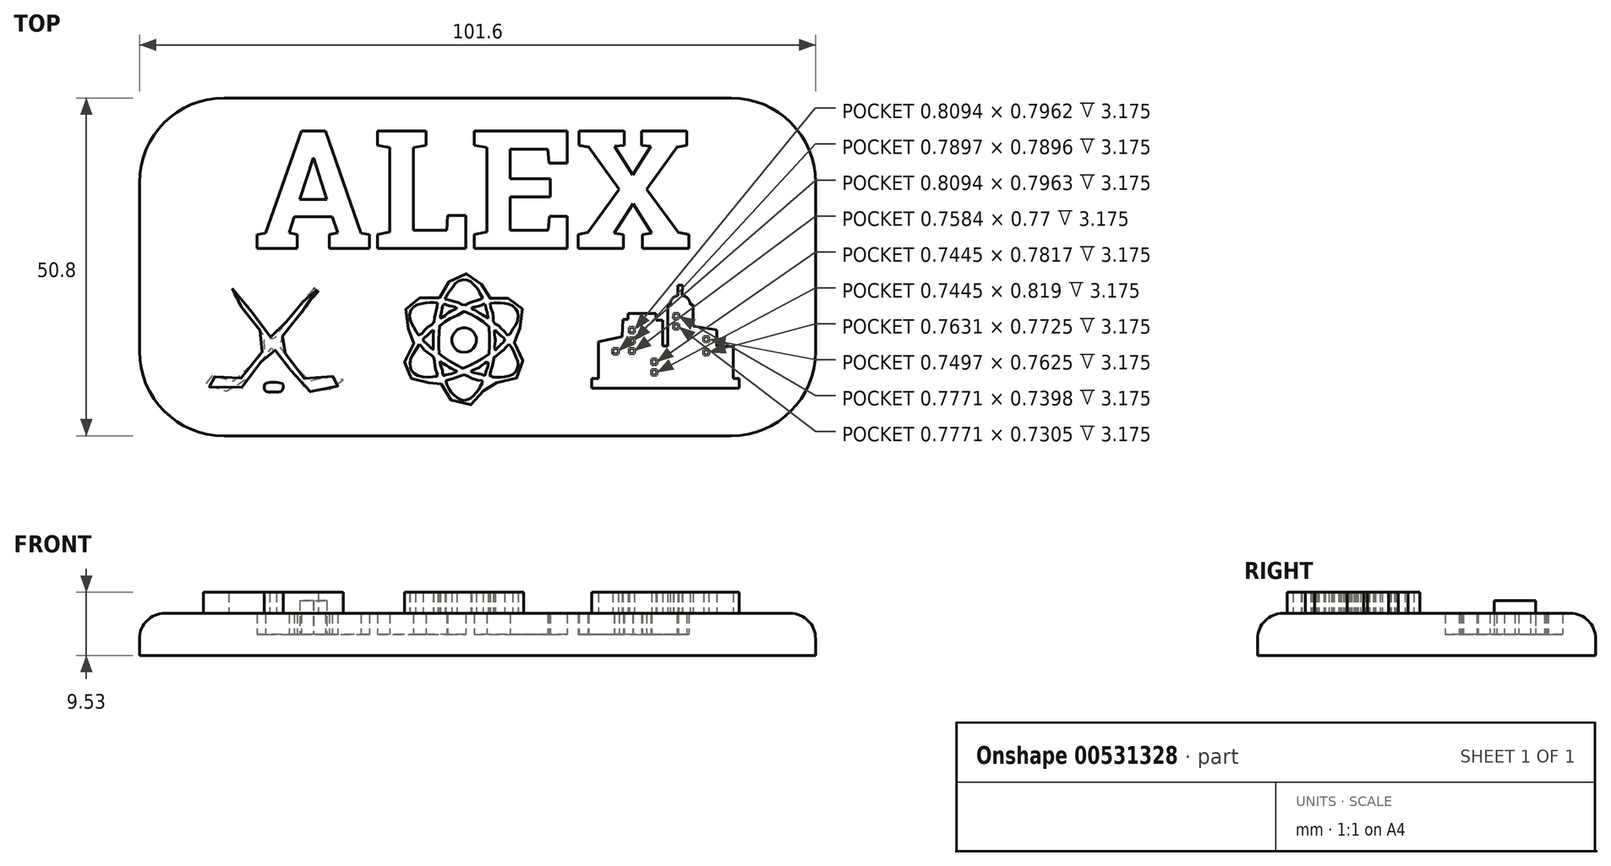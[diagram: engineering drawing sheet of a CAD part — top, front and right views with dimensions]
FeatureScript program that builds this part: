
annotation { "Feature Type Name" : "Feature", "Feature Type Description" : "" }
export const myFeature = defineFeature(function(context is Context, id is Id, definition is map)
    precondition{}
    {
        {
            var Q0;
            Q0=qCreatedBy(makeId("Top.planeOp"),FACE);
            var sketch = newSketch(context, id + "F0", { "sketchPlane" : qUnion([Q0])});
            skLineSegment(sketch, "E0", {"start": v(-38.91, 22.63) * mm, "end": v(37.29, 22.63) * mm});
            skLineSegment(sketch, "E1", {"start": v(49.99, 9.93) * mm, "end": v(49.99, -15.47) * mm});
            skLineSegment(sketch, "E2", {"start": v(-51.61, 9.93) * mm, "end": v(-51.61, -15.47) * mm});
            skLineSegment(sketch, "E3", {"start": v(-38.91, -28.17) * mm, "end": v(37.29, -28.17) * mm});
            skPoint(sketch, "E4.visualSharp", {"position": v(-51.61, 22.63) * mm});
            skArc(sketch, "E4.filletArc", {"start": v(-38.91, 22.63) * mm, "mid": v(-47.9, 18.91) * mm, "end": v(-51.61, 9.93) * mm});
            skPoint(sketch, "E5.visualSharp", {"position": v(49.99, 22.63) * mm});
            skArc(sketch, "E5.filletArc", {"start": v(49.99, 9.93) * mm, "mid": v(46.27, 18.91) * mm, "end": v(37.29, 22.63) * mm});
            skPoint(sketch, "E6.visualSharp", {"position": v(49.99, -28.17) * mm});
            skArc(sketch, "E6.filletArc", {"start": v(37.29, -28.17) * mm, "mid": v(46.27, -24.45) * mm, "end": v(49.99, -15.47) * mm});
            skPoint(sketch, "E7.visualSharp", {"position": v(-51.61, -28.17) * mm});
            skArc(sketch, "E7.filletArc", {"start": v(-51.61, -15.47) * mm, "mid": v(-47.9, -24.45) * mm, "end": v(-38.91, -28.17) * mm});
            skText(sketch, "E8", { "text": "ALEX", "fontName": "RobotoSlab-Bold.ttf"});
            const initialGuessF0  = {"E8": [-0.03442, 0, 1, 0, 0.0179]};
            skSetInitialGuess(sketch, initialGuessF0);
            skSolve(sketch);
        }
        {
            var Q0;
            Q0=makeQuery(id+"F0.imprint","IMPRINT",FACE,{"disambiguationData":[TD([[makeQuery(id+"F0.imprint","IMPRINT",EDGE,{"derivedFrom":sQuery(id+"F0.wireOp",EDGE,"E0")}),-1.0]])]});
            extrude(context, id + "F1", {"entities" : qUnion([Q0]), "depth" : 6.35 * mm, "offsetDistance" : 25.4 * mm});
        }
        {
            var Q0;
            Q0=makeQuery(id+"F1.opExtrude","CAP_EDGE",EDGE,{"disambiguationData":[OSD([sQuery(id+"F0.wireOp",EDGE,"E4.filletArc")])],"isStart":false});
            var Q1;
            Q1=makeQuery(id+"F1.opExtrude","CAP_EDGE",EDGE,{"disambiguationData":[OSD([sQuery(id+"F0.wireOp",EDGE,"E0")])],"isStart":false});
            var Q2;
            Q2=makeQuery(id+"F1.opExtrude","CAP_EDGE",EDGE,{"disambiguationData":[OSD([sQuery(id+"F0.wireOp",EDGE,"E5.filletArc")])],"isStart":false});
            var Q3;
            Q3=makeQuery(id+"F1.opExtrude","CAP_EDGE",EDGE,{"disambiguationData":[OSD([sQuery(id+"F0.wireOp",EDGE,"E1")])],"isStart":false});
            var Q4;
            Q4=makeQuery(id+"F1.opExtrude","CAP_EDGE",EDGE,{"disambiguationData":[OSD([sQuery(id+"F0.wireOp",EDGE,"E6.filletArc")])],"isStart":false});
            var Q5;
            Q5=makeQuery(id+"F1.opExtrude","CAP_EDGE",EDGE,{"disambiguationData":[OSD([sQuery(id+"F0.wireOp",EDGE,"E3")])],"isStart":false});
            var Q6;
            Q6=makeQuery(id+"F1.opExtrude","CAP_EDGE",EDGE,{"disambiguationData":[OSD([sQuery(id+"F0.wireOp",EDGE,"E7.filletArc")])],"isStart":false});
            var Q7;
            Q7=makeQuery(id+"F1.opExtrude","CAP_EDGE",EDGE,{"disambiguationData":[OSD([sQuery(id+"F0.wireOp",EDGE,"E2")])],"isStart":false});
            fillet(context, id + "F2", {"entities" : qUnion([Q0, Q1, Q2, Q3, Q4, Q5, Q6, Q7]), "radius" : 3.8 * mm, "tangentPropagation" : true, "allowEdgeOverflow" : false});
        }
        {
            var Q0;
            Q0=makeQuery(id+"F1.opExtrude","CAP_FACE",FACE,{"disambiguationData":[OSD([sQuery(id+"F0.wireOp",EDGE,"E0"),sQuery(id+"F0.wireOp",EDGE,"E1"),sQuery(id+"F0.wireOp",EDGE,"E2"),sQuery(id+"F0.wireOp",EDGE,"E3"),sQuery(id+"F0.wireOp",EDGE,"E4.filletArc"),sQuery(id+"F0.wireOp",EDGE,"E5.filletArc"),sQuery(id+"F0.wireOp",EDGE,"E6.filletArc"),sQuery(id+"F0.wireOp",EDGE,"E7.filletArc"),sQuery(id+"F0.wireOp",EDGE,"E8.sketch_text.stroke-0"),sQuery(id+"F0.wireOp",EDGE,"E8.sketch_text.stroke-1"),sQuery(id+"F0.wireOp",EDGE,"E8.sketch_text.stroke-2"),sQuery(id+"F0.wireOp",EDGE,"E8.sketch_text.stroke-3"),sQuery(id+"F0.wireOp",EDGE,"E8.sketch_text.stroke-4"),sQuery(id+"F0.wireOp",EDGE,"E8.sketch_text.stroke-5"),sQuery(id+"F0.wireOp",EDGE,"E8.sketch_text.stroke-6"),sQuery(id+"F0.wireOp",EDGE,"E8.sketch_text.stroke-7"),sQuery(id+"F0.wireOp",EDGE,"E8.sketch_text.stroke-8"),sQuery(id+"F0.wireOp",EDGE,"E8.sketch_text.stroke-9"),sQuery(id+"F0.wireOp",EDGE,"E8.sketch_text.stroke-10"),sQuery(id+"F0.wireOp",EDGE,"E8.sketch_text.stroke-11"),sQuery(id+"F0.wireOp",EDGE,"E8.sketch_text.stroke-12"),sQuery(id+"F0.wireOp",EDGE,"E8.sketch_text.stroke-13"),sQuery(id+"F0.wireOp",EDGE,"E8.sketch_text.stroke-14"),sQuery(id+"F0.wireOp",EDGE,"E8.sketch_text.stroke-15"),sQuery(id+"F0.wireOp",EDGE,"E8.sketch_text.stroke-20"),sQuery(id+"F0.wireOp",EDGE,"E8.sketch_text.stroke-21"),sQuery(id+"F0.wireOp",EDGE,"E8.sketch_text.stroke-22"),sQuery(id+"F0.wireOp",EDGE,"E8.sketch_text.stroke-23"),sQuery(id+"F0.wireOp",EDGE,"E8.sketch_text.stroke-24"),sQuery(id+"F0.wireOp",EDGE,"E8.sketch_text.stroke-25"),sQuery(id+"F0.wireOp",EDGE,"E8.sketch_text.stroke-26"),sQuery(id+"F0.wireOp",EDGE,"E8.sketch_text.stroke-27"),sQuery(id+"F0.wireOp",EDGE,"E8.sketch_text.stroke-28"),sQuery(id+"F0.wireOp",EDGE,"E8.sketch_text.stroke-29"),sQuery(id+"F0.wireOp",EDGE,"E8.sketch_text.stroke-30"),sQuery(id+"F0.wireOp",EDGE,"E8.sketch_text.stroke-31"),sQuery(id+"F0.wireOp",EDGE,"E8.sketch_text.stroke-32"),sQuery(id+"F0.wireOp",EDGE,"E8.sketch_text.stroke-33"),sQuery(id+"F0.wireOp",EDGE,"E8.sketch_text.stroke-34"),sQuery(id+"F0.wireOp",EDGE,"E8.sketch_text.stroke-35"),sQuery(id+"F0.wireOp",EDGE,"E8.sketch_text.stroke-36"),sQuery(id+"F0.wireOp",EDGE,"E8.sketch_text.stroke-37"),sQuery(id+"F0.wireOp",EDGE,"E8.sketch_text.stroke-38"),sQuery(id+"F0.wireOp",EDGE,"E8.sketch_text.stroke-39"),sQuery(id+"F0.wireOp",EDGE,"E8.sketch_text.stroke-40"),sQuery(id+"F0.wireOp",EDGE,"E8.sketch_text.stroke-41"),sQuery(id+"F0.wireOp",EDGE,"E8.sketch_text.stroke-42"),sQuery(id+"F0.wireOp",EDGE,"E8.sketch_text.stroke-43"),sQuery(id+"F0.wireOp",EDGE,"E8.sketch_text.stroke-44"),sQuery(id+"F0.wireOp",EDGE,"E8.sketch_text.stroke-45"),sQuery(id+"F0.wireOp",EDGE,"E8.sketch_text.stroke-46"),sQuery(id+"F0.wireOp",EDGE,"E8.sketch_text.stroke-47"),sQuery(id+"F0.wireOp",EDGE,"E8.sketch_text.stroke-48"),sQuery(id+"F0.wireOp",EDGE,"E8.sketch_text.stroke-49"),sQuery(id+"F0.wireOp",EDGE,"E8.sketch_text.stroke-50"),sQuery(id+"F0.wireOp",EDGE,"E8.sketch_text.stroke-51"),sQuery(id+"F0.wireOp",EDGE,"E8.sketch_text.stroke-52"),sQuery(id+"F0.wireOp",EDGE,"E8.sketch_text.stroke-53"),sQuery(id+"F0.wireOp",EDGE,"E8.sketch_text.stroke-54"),sQuery(id+"F0.wireOp",EDGE,"E8.sketch_text.stroke-55"),sQuery(id+"F0.wireOp",EDGE,"E8.sketch_text.stroke-56"),sQuery(id+"F0.wireOp",EDGE,"E8.sketch_text.stroke-57"),sQuery(id+"F0.wireOp",EDGE,"E8.sketch_text.stroke-58"),sQuery(id+"F0.wireOp",EDGE,"E8.sketch_text.stroke-59"),sQuery(id+"F0.wireOp",EDGE,"E8.sketch_text.stroke-60"),sQuery(id+"F0.wireOp",EDGE,"E8.sketch_text.stroke-61"),sQuery(id+"F0.wireOp",EDGE,"E8.sketch_text.stroke-62"),sQuery(id+"F0.wireOp",EDGE,"E8.sketch_text.stroke-63"),sQuery(id+"F0.wireOp",EDGE,"E8.sketch_text.stroke-64"),sQuery(id+"F0.wireOp",EDGE,"E8.sketch_text.stroke-65"),sQuery(id+"F0.wireOp",EDGE,"E8.sketch_text.stroke-66"),sQuery(id+"F0.wireOp",EDGE,"E8.sketch_text.stroke-67"),sQuery(id+"F0.wireOp",EDGE,"E8.sketch_text.stroke-68"),sQuery(id+"F0.wireOp",EDGE,"E8.sketch_text.stroke-69"),sQuery(id+"F0.wireOp",EDGE,"E8.sketch_text.stroke-70"),sQuery(id+"F0.wireOp",EDGE,"E8.sketch_text.stroke-71"),sQuery(id+"F0.wireOp",EDGE,"E8.sketch_text.stroke-72"),sQuery(id+"F0.wireOp",EDGE,"E8.sketch_text.stroke-73"),sQuery(id+"F0.wireOp",EDGE,"E8.sketch_text.stroke-74"),sQuery(id+"F0.wireOp",EDGE,"E8.sketch_text.stroke-75"),sQuery(id+"F0.wireOp",EDGE,"E8.sketch_text.stroke-76"),sQuery(id+"F0.wireOp",EDGE,"E8.sketch_text.stroke-77"),sQuery(id+"F0.wireOp",EDGE,"E8.sketch_text.stroke-78"),sQuery(id+"F0.wireOp",EDGE,"E8.sketch_text.stroke-79"),sQuery(id+"F0.wireOp",EDGE,"E8.sketch_text.stroke-80"),sQuery(id+"F0.wireOp",EDGE,"E8.sketch_text.stroke-81"),sQuery(id+"F0.wireOp",EDGE,"E8.sketch_text.stroke-82"),sQuery(id+"F0.wireOp",EDGE,"E8.sketch_text.stroke-83"),sQuery(id+"F0.wireOp",EDGE,"E8.sketch_text.stroke-84")])],"isStart":false});
            var sketch = newSketch(context, id + "F3", { "sketchPlane" : qUnion([Q0])});
            skFitSpline(sketch, "E9", {"points": [v(-37.72, -6.03) * mm, v(-38.01, -6.2) * mm, v(-38.19, -6.38) * mm, v(-37.9, -6.81) * mm, v(-37.17, -7.71) * mm, v(-36.2, -8.88) * mm, v(-35.54, -9.72) * mm, v(-35.1, -10.42) * mm, v(-34.44, -11.12) * mm, v(-33.33, -12.54) * mm, v(-32.52, -13.53) * mm, v(-32.05, -14.11) * mm, v(-32.23, -14.49) * mm, v(-33.13, -15.5) * mm, v(-34.23, -16.79) * mm, v(-34.73, -17.37) * mm, v(-36, -18.94) * mm, v(-36.65, -19.84) * mm, v(-37.34, -19.95) * mm, v(-38.4, -19.9) * mm, v(-39.7, -19.49) * mm, v(-40.98, -19.08) * mm, v(-41.53, -19.02) * mm, v(-41.88, -19.32) * mm, v(-41.94, -20.16) * mm, v(-41.21, -20.77) * mm, v(-40.22, -21.09) * mm, v(-38.65, -21.44) * mm, v(-36.88, -21.5) * mm, v(-35.28, -19.55) * mm, v(-34.58, -18.7) * mm, v(-33.83, -17.77) * mm, v(-33.36, -17.1) * mm, v(-32.8, -16.35) * mm, v(-32.34, -15.71) * mm, v(-31.97, -15.22) * mm, v(-31.59, -14.84) * mm, v(-31.18, -15.33) * mm, v(-30.77, -15.94) * mm, v(-29.93, -16.96) * mm, v(-29.44, -17.6) * mm, v(-29.03, -18.18) * mm, v(-28.53, -18.76) * mm, v(-27.95, -19.46) * mm, v(-26.73, -20.91) * mm, v(-26.24, -21.47) * mm, v(-24.29, -21.4) * mm, v(-23.39, -21.3) * mm, v(-22.6, -21) * mm, v(-21.96, -20.77) * mm, v(-21.47, -20.33) * mm, v(-21.05, -19.8) * mm, v(-21.05, -19.4) * mm, v(-21.41, -19.08) * mm, v(-21.9, -19.05) * mm, v(-23.07, -19.37) * mm, v(-24.29, -19.75) * mm, v(-25.2, -19.9) * mm, v(-26.38, -19.87) * mm, v(-27.6, -18.62) * mm, v(-28.74, -17.1) * mm, v(-29.15, -16.64) * mm, v(-29.64, -15.88) * mm, v(-30.4, -14.93) * mm, v(-30.92, -14.29) * mm, v(-31.03, -14.17) * mm, v(-30.66, -13.8) * mm, v(-30.3, -13.36) * mm, v(-29.67, -12.66) * mm, v(-29.06, -11.87) * mm, v(-27.7, -10.13) * mm, v(-27.28, -9.6) * mm, v(-26.32, -8.35) * mm, v(-25.69, -7.48) * mm, v(-24.76, -6.38) * mm, v(-24.96, -6.32) * mm, v(-25.2, -6.12) * mm, v(-25.4, -6) * mm, v(-25.77, -6.44) * mm, v(-26.03, -6.76) * mm, v(-26.41, -7.13) * mm, v(-26.94, -7.89) * mm, v(-27.28, -8.35) * mm, v(-27.78, -8.9) * mm, v(-28.42, -9.7) * mm, v(-29.23, -10.65) * mm, v(-29.9, -11.44) * mm, v(-30.45, -12.16) * mm, v(-31.03, -12.98) * mm, v(-31.56, -13.73) * mm, v(-32.29, -12.72) * mm, v(-33.42, -11.3) * mm, v(-34.09, -10.39) * mm, v(-34.58, -9.7) * mm, v(-34.9, -9.26) * mm, v(-35.66, -8.27) * mm, v(-36.76, -7.08) * mm, v(-37.72, -6.03) * mm]});
            skFitSpline(sketch, "E10", {"points": [v(-31.64, -20.12) * mm, v(-32.3, -20.19) * mm, v(-32.82, -20.46) * mm, v(-32.85, -21.09) * mm, v(-32.58, -21.47) * mm, v(-31.85, -21.6) * mm, v(-30.78, -21.57) * mm, v(-30.16, -21.33) * mm, v(-30.05, -20.4) * mm, v(-30.33, -20.26) * mm, v(-31.02, -20.12) * mm, v(-31.64, -20.12) * mm]});
            skSolve(sketch);
        }
        {
            var Q0;
            Q0 = qSketchRegion(id + "F3", true);
            extrude(context, id + "F4", {"entities" : qUnion([Q0]), "operationType" : NewBodyOperationType.ADD, "depth" : 3.17 * mm, "offsetDistance" : 25.4 * mm});
        }
        {
            var Q0;
            Q0=makeQuery(id+"F1.opExtrude","CAP_FACE",FACE,{"disambiguationData":[OSD([sQuery(id+"F0.wireOp",EDGE,"E0"),sQuery(id+"F0.wireOp",EDGE,"E1"),sQuery(id+"F0.wireOp",EDGE,"E2"),sQuery(id+"F0.wireOp",EDGE,"E3"),sQuery(id+"F0.wireOp",EDGE,"E4.filletArc"),sQuery(id+"F0.wireOp",EDGE,"E5.filletArc"),sQuery(id+"F0.wireOp",EDGE,"E6.filletArc"),sQuery(id+"F0.wireOp",EDGE,"E7.filletArc"),sQuery(id+"F0.wireOp",EDGE,"E8.sketch_text.stroke-0"),sQuery(id+"F0.wireOp",EDGE,"E8.sketch_text.stroke-1"),sQuery(id+"F0.wireOp",EDGE,"E8.sketch_text.stroke-2"),sQuery(id+"F0.wireOp",EDGE,"E8.sketch_text.stroke-3"),sQuery(id+"F0.wireOp",EDGE,"E8.sketch_text.stroke-4"),sQuery(id+"F0.wireOp",EDGE,"E8.sketch_text.stroke-5"),sQuery(id+"F0.wireOp",EDGE,"E8.sketch_text.stroke-6"),sQuery(id+"F0.wireOp",EDGE,"E8.sketch_text.stroke-7"),sQuery(id+"F0.wireOp",EDGE,"E8.sketch_text.stroke-8"),sQuery(id+"F0.wireOp",EDGE,"E8.sketch_text.stroke-9"),sQuery(id+"F0.wireOp",EDGE,"E8.sketch_text.stroke-10"),sQuery(id+"F0.wireOp",EDGE,"E8.sketch_text.stroke-11"),sQuery(id+"F0.wireOp",EDGE,"E8.sketch_text.stroke-12"),sQuery(id+"F0.wireOp",EDGE,"E8.sketch_text.stroke-13"),sQuery(id+"F0.wireOp",EDGE,"E8.sketch_text.stroke-14"),sQuery(id+"F0.wireOp",EDGE,"E8.sketch_text.stroke-15"),sQuery(id+"F0.wireOp",EDGE,"E8.sketch_text.stroke-20"),sQuery(id+"F0.wireOp",EDGE,"E8.sketch_text.stroke-21"),sQuery(id+"F0.wireOp",EDGE,"E8.sketch_text.stroke-22"),sQuery(id+"F0.wireOp",EDGE,"E8.sketch_text.stroke-23"),sQuery(id+"F0.wireOp",EDGE,"E8.sketch_text.stroke-24"),sQuery(id+"F0.wireOp",EDGE,"E8.sketch_text.stroke-25"),sQuery(id+"F0.wireOp",EDGE,"E8.sketch_text.stroke-26"),sQuery(id+"F0.wireOp",EDGE,"E8.sketch_text.stroke-27"),sQuery(id+"F0.wireOp",EDGE,"E8.sketch_text.stroke-28"),sQuery(id+"F0.wireOp",EDGE,"E8.sketch_text.stroke-29"),sQuery(id+"F0.wireOp",EDGE,"E8.sketch_text.stroke-30"),sQuery(id+"F0.wireOp",EDGE,"E8.sketch_text.stroke-31"),sQuery(id+"F0.wireOp",EDGE,"E8.sketch_text.stroke-32"),sQuery(id+"F0.wireOp",EDGE,"E8.sketch_text.stroke-33"),sQuery(id+"F0.wireOp",EDGE,"E8.sketch_text.stroke-34"),sQuery(id+"F0.wireOp",EDGE,"E8.sketch_text.stroke-35"),sQuery(id+"F0.wireOp",EDGE,"E8.sketch_text.stroke-36"),sQuery(id+"F0.wireOp",EDGE,"E8.sketch_text.stroke-37"),sQuery(id+"F0.wireOp",EDGE,"E8.sketch_text.stroke-38"),sQuery(id+"F0.wireOp",EDGE,"E8.sketch_text.stroke-39"),sQuery(id+"F0.wireOp",EDGE,"E8.sketch_text.stroke-40"),sQuery(id+"F0.wireOp",EDGE,"E8.sketch_text.stroke-41"),sQuery(id+"F0.wireOp",EDGE,"E8.sketch_text.stroke-42"),sQuery(id+"F0.wireOp",EDGE,"E8.sketch_text.stroke-43"),sQuery(id+"F0.wireOp",EDGE,"E8.sketch_text.stroke-44"),sQuery(id+"F0.wireOp",EDGE,"E8.sketch_text.stroke-45"),sQuery(id+"F0.wireOp",EDGE,"E8.sketch_text.stroke-46"),sQuery(id+"F0.wireOp",EDGE,"E8.sketch_text.stroke-47"),sQuery(id+"F0.wireOp",EDGE,"E8.sketch_text.stroke-48"),sQuery(id+"F0.wireOp",EDGE,"E8.sketch_text.stroke-49"),sQuery(id+"F0.wireOp",EDGE,"E8.sketch_text.stroke-50"),sQuery(id+"F0.wireOp",EDGE,"E8.sketch_text.stroke-51"),sQuery(id+"F0.wireOp",EDGE,"E8.sketch_text.stroke-52"),sQuery(id+"F0.wireOp",EDGE,"E8.sketch_text.stroke-53"),sQuery(id+"F0.wireOp",EDGE,"E8.sketch_text.stroke-54"),sQuery(id+"F0.wireOp",EDGE,"E8.sketch_text.stroke-55"),sQuery(id+"F0.wireOp",EDGE,"E8.sketch_text.stroke-56"),sQuery(id+"F0.wireOp",EDGE,"E8.sketch_text.stroke-57"),sQuery(id+"F0.wireOp",EDGE,"E8.sketch_text.stroke-58"),sQuery(id+"F0.wireOp",EDGE,"E8.sketch_text.stroke-59"),sQuery(id+"F0.wireOp",EDGE,"E8.sketch_text.stroke-60"),sQuery(id+"F0.wireOp",EDGE,"E8.sketch_text.stroke-61"),sQuery(id+"F0.wireOp",EDGE,"E8.sketch_text.stroke-62"),sQuery(id+"F0.wireOp",EDGE,"E8.sketch_text.stroke-63"),sQuery(id+"F0.wireOp",EDGE,"E8.sketch_text.stroke-64"),sQuery(id+"F0.wireOp",EDGE,"E8.sketch_text.stroke-65"),sQuery(id+"F0.wireOp",EDGE,"E8.sketch_text.stroke-66"),sQuery(id+"F0.wireOp",EDGE,"E8.sketch_text.stroke-67"),sQuery(id+"F0.wireOp",EDGE,"E8.sketch_text.stroke-68"),sQuery(id+"F0.wireOp",EDGE,"E8.sketch_text.stroke-69"),sQuery(id+"F0.wireOp",EDGE,"E8.sketch_text.stroke-70"),sQuery(id+"F0.wireOp",EDGE,"E8.sketch_text.stroke-71"),sQuery(id+"F0.wireOp",EDGE,"E8.sketch_text.stroke-72"),sQuery(id+"F0.wireOp",EDGE,"E8.sketch_text.stroke-73"),sQuery(id+"F0.wireOp",EDGE,"E8.sketch_text.stroke-74"),sQuery(id+"F0.wireOp",EDGE,"E8.sketch_text.stroke-75"),sQuery(id+"F0.wireOp",EDGE,"E8.sketch_text.stroke-76"),sQuery(id+"F0.wireOp",EDGE,"E8.sketch_text.stroke-77"),sQuery(id+"F0.wireOp",EDGE,"E8.sketch_text.stroke-78"),sQuery(id+"F0.wireOp",EDGE,"E8.sketch_text.stroke-79"),sQuery(id+"F0.wireOp",EDGE,"E8.sketch_text.stroke-80"),sQuery(id+"F0.wireOp",EDGE,"E8.sketch_text.stroke-81"),sQuery(id+"F0.wireOp",EDGE,"E8.sketch_text.stroke-82"),sQuery(id+"F0.wireOp",EDGE,"E8.sketch_text.stroke-83"),sQuery(id+"F0.wireOp",EDGE,"E8.sketch_text.stroke-84")])],"isStart":false});
            var sketch = newSketch(context, id + "F5", { "sketchPlane" : qUnion([Q0])});
            skFitSpline(sketch, "E11", {"points": [v(-3.09, -11.93) * mm, v(-3.65, -12.08) * mm, v(-3.98, -12.34) * mm, v(-4.35, -12.71) * mm, v(-4.65, -13.42) * mm, v(-4.58, -14.35) * mm, v(-4.17, -15.06) * mm, v(-3.76, -15.4) * mm, v(-3.01, -15.58) * mm, v(-2.23, -15.5) * mm, v(-1.56, -15.13) * mm, v(-1.12, -14.42) * mm, v(-1, -13.6) * mm, v(-1.15, -12.97) * mm, v(-1.49, -12.49) * mm, v(-1.93, -12.15) * mm, v(-2.42, -11.97) * mm, v(-3.09, -11.93) * mm]});
            skFitSpline(sketch, "E12", {"points": [v(-2.87, -9.44) * mm, v(-2.08, -9.73) * mm, v(-1.52, -10.07) * mm, v(-0.9, -10.37) * mm, v(0, -10.96) * mm, v(0.78, -11.48) * mm, v(0.97, -12.3) * mm, v(0.97, -13.83) * mm, v(0.97, -15.06) * mm, v(0.86, -15.91) * mm, v(0, -16.5) * mm, v(-0.74, -16.92) * mm, v(-1.79, -17.48) * mm, v(-2.5, -17.85) * mm, v(-2.83, -18.04) * mm, v(-3.39, -17.81) * mm, v(-4.1, -17.44) * mm, v(-4.8, -17.03) * mm, v(-5.62, -16.58) * mm, v(-6.14, -16.17) * mm, v(-6.55, -15.95) * mm, v(-6.59, -15.24) * mm, v(-6.66, -14.54) * mm, v(-6.62, -13.83) * mm, v(-6.62, -12.97) * mm, v(-6.59, -12.49) * mm, v(-6.59, -11.74) * mm, v(-6.25, -11.37) * mm, v(-5.58, -10.93) * mm, v(-5.06, -10.63) * mm, v(-4.47, -10.33) * mm, v(-3.42, -9.77) * mm, v(-2.87, -9.44) * mm]});
            skFitSpline(sketch, "E13", {"points": [v(-5.92, -8.43) * mm, v(-5.1, -8.58) * mm, v(-3.94, -8.95) * mm, v(-4.58, -9.29) * mm, v(-5.47, -9.88) * mm, v(-6.36, -10.48) * mm, v(-6.36, -10.1) * mm, v(-6.22, -9.51) * mm, v(-5.92, -8.43) * mm]});
            skFitSpline(sketch, "E14", {"points": [v(0.26, -8.36) * mm, v(0, -8.4) * mm, v(-0.56, -8.62) * mm, v(-1.08, -8.73) * mm, v(-1.71, -8.99) * mm, v(-1.04, -9.36) * mm, v(-0.37, -9.8) * mm, v(0, -10) * mm, v(0.75, -10.48) * mm, v(0.75, -10.26) * mm, v(0.63, -9.59) * mm, v(0.49, -9.03) * mm, v(0.26, -8.36) * mm]});
            skFitSpline(sketch, "E15", {"points": [v(1.79, -12.27) * mm, v(2.27, -12.71) * mm, v(2.87, -13.23) * mm, v(3.28, -13.68) * mm, v(2.76, -14.39) * mm, v(2.2, -14.9) * mm, v(1.83, -15.28) * mm, v(1.83, -14.13) * mm, v(1.83, -13.38) * mm, v(1.79, -12.27) * mm]});
            skFitSpline(sketch, "E16", {"points": [v(-1.82, -18.44) * mm, v(-1.23, -18.7) * mm, v(-0.45, -18.9) * mm, v(0, -19) * mm, v(0.3, -19.08) * mm, v(0.37, -18.74) * mm, v(0.6, -18.18) * mm, v(0.7, -17.85) * mm, v(0.75, -17.1) * mm, v(0, -17.48) * mm, v(-0.52, -17.85) * mm, v(-1.12, -18.15) * mm, v(-1.82, -18.44) * mm]});
            skFitSpline(sketch, "E17", {"points": [v(-6.48, -16.96) * mm, v(-5.84, -17.37) * mm, v(-5.25, -17.74) * mm, v(-4.43, -18.22) * mm, v(-3.94, -18.44) * mm, v(-4.32, -18.7) * mm, v(-5.14, -18.9) * mm, v(-5.77, -19.08) * mm, v(-5.92, -19.11) * mm, v(-6.07, -18.52) * mm, v(-6.22, -17.89) * mm, v(-6.48, -16.96) * mm]});
            skFitSpline(sketch, "E18", {"points": [v(-7.48, -12.27) * mm, v(-8.19, -12.9) * mm, v(-8.56, -13.23) * mm, v(-9, -13.68) * mm, v(-8.6, -14.2) * mm, v(-8.19, -14.57) * mm, v(-7.82, -14.9) * mm, v(-7.52, -15.17) * mm, v(-7.48, -14.42) * mm, v(-7.48, -13.53) * mm, v(-7.44, -12.86) * mm, v(-7.48, -12.27) * mm]});
            skFitSpline(sketch, "E19", {"points": [v(-5.66, -7.61) * mm, v(-5.06, -7.76) * mm, v(-4.32, -7.98) * mm, v(-3.39, -8.28) * mm, v(-2.94, -8.54) * mm, v(-2.34, -8.32) * mm, v(-1.67, -8.06) * mm, v(-1.04, -7.87) * mm, v(-0.33, -7.61) * mm, v(0, -7.57) * mm, v(-0.45, -6.8) * mm, v(-0.67, -6.27) * mm, v(-1, -5.79) * mm, v(-1.38, -5.42) * mm, v(-1.86, -4.97) * mm, v(-2.42, -4.75) * mm, v(-2.98, -4.7) * mm, v(-3.8, -4.93) * mm, v(-4.24, -5.38) * mm, v(-4.8, -6.12) * mm, v(-5.17, -6.64) * mm, v(-5.66, -7.61) * mm]});
            skFitSpline(sketch, "E20", {"points": [v(-2.87, -18.97) * mm, v(-3.57, -19.23) * mm, v(-4.2, -19.45) * mm, v(-5.02, -19.71) * mm, v(-5.55, -19.82) * mm, v(-5.32, -20.72) * mm, v(-4.88, -21.5) * mm, v(-4.17, -22.2) * mm, v(-3.2, -22.8) * mm, v(-2.34, -22.76) * mm, v(-1.56, -22.28) * mm, v(-1.08, -21.8) * mm, v(-0.56, -21.05) * mm, v(-0.37, -20.64) * mm, v(0, -19.97) * mm, v(-0.67, -19.82) * mm, v(-2.05, -19.3) * mm, v(-2.87, -18.97) * mm]});
            skFitSpline(sketch, "E21", {"points": [v(-6.81, -8.2) * mm, v(-7.6, -8.13) * mm, v(-8.41, -8.13) * mm, v(-9.42, -8.32) * mm, v(-10.16, -8.58) * mm, v(-10.9, -9.4) * mm, v(-11.02, -10.44) * mm, v(-10.72, -11.22) * mm, v(-10.16, -12.3) * mm, v(-9.57, -13.05) * mm, v(-8.78, -12.3) * mm, v(-8.15, -11.7) * mm, v(-7.4, -11.22) * mm, v(-7.3, -10.33) * mm, v(-7.07, -9.62) * mm, v(-6.96, -8.92) * mm, v(-6.81, -8.2) * mm]});
            skFitSpline(sketch, "E22", {"points": [v(1.12, -8.25) * mm, v(1.83, -8.17) * mm, v(2.2, -8.17) * mm, v(2.8, -8.17) * mm, v(3.76, -8.32) * mm, v(4.54, -8.65) * mm, v(5.1, -9.32) * mm, v(5.29, -10.14) * mm, v(5.03, -11.37) * mm, v(4.54, -12.04) * mm, v(3.84, -13.08) * mm, v(3.39, -12.67) * mm, v(2.68, -11.97) * mm, v(2.2, -11.48) * mm, v(1.64, -11.15) * mm, v(1.56, -10.33) * mm, v(1.38, -9.4) * mm, v(1.12, -8.25) * mm]});
            skFitSpline(sketch, "E23", {"points": [v(-9.57, -14.42) * mm, v(-9.2, -14.8) * mm, v(-8.75, -15.28) * mm, v(-8.3, -15.62) * mm, v(-7.6, -16.17) * mm, v(-7.4, -16.36) * mm, v(-7.26, -17.1) * mm, v(-7.18, -17.81) * mm, v(-6.96, -18.6) * mm, v(-6.81, -19.15) * mm, v(-7.3, -19.26) * mm, v(-7.9, -19.34) * mm, v(-8.97, -19.3) * mm, v(-9.98, -19) * mm, v(-10.46, -18.7) * mm, v(-10.76, -18.26) * mm, v(-10.94, -17.7) * mm, v(-10.9, -16.8) * mm, v(-10.6, -16.03) * mm, v(-10.24, -15.43) * mm, v(-9.86, -14.87) * mm, v(-9.57, -14.42) * mm]});
            skFitSpline(sketch, "E24", {"points": [v(3.87, -14.39) * mm, v(3.5, -14.8) * mm, v(2.98, -15.32) * mm, v(2.3, -15.91) * mm, v(1.68, -16.36) * mm, v(1.53, -17.14) * mm, v(1.3, -18.1) * mm, v(1.04, -19.19) * mm, v(1.86, -19.34) * mm, v(2.64, -19.34) * mm, v(3.1, -19.3) * mm, v(3.87, -19.19) * mm, v(4.73, -18.74) * mm, v(5.1, -18.18) * mm, v(5.25, -17.74) * mm, v(5.25, -17.1) * mm, v(4.99, -16.4) * mm, v(4.58, -15.43) * mm, v(3.87, -14.39) * mm]});
            skFitSpline(sketch, "E25", {"points": [v(-6.51, -7.39) * mm, v(-6.14, -6.64) * mm, v(-5.7, -5.75) * mm, v(-5.06, -4.93) * mm, v(-4.28, -4.22) * mm, v(-3.24, -3.85) * mm, v(-2.2, -3.85) * mm, v(-1.41, -4.3) * mm, v(-0.56, -4.93) * mm, v(0, -5.86) * mm, v(0.37, -6.5) * mm, v(0.82, -7.46) * mm, v(1.23, -7.46) * mm, v(2.3, -7.28) * mm, v(3.1, -7.39) * mm, v(4.1, -7.57) * mm, v(5.1, -8.1) * mm, v(5.59, -8.5) * mm, v(6, -9.32) * mm, v(6.07, -10.52) * mm, v(5.73, -11.56) * mm, v(5.36, -12.45) * mm, v(4.7, -13.46) * mm, v(4.47, -13.8) * mm, v(4.88, -14.31) * mm, v(5.51, -15.47) * mm, v(5.88, -16.43) * mm, v(6.1, -17.51) * mm, v(5.8, -18.56) * mm, v(5.21, -19.38) * mm, v(4.1, -19.97) * mm, v(2.87, -20.16) * mm, v(1.79, -20.16) * mm, v(0.82, -20.05) * mm, v(0.6, -20.46) * mm, v(0, -21.5) * mm, v(-0.56, -22.4) * mm, v(-1.34, -23.17) * mm, v(-2.12, -23.63) * mm, v(-3.65, -23.63) * mm, v(-4.69, -22.91) * mm, v(-5.55, -21.9) * mm, v(-5.88, -21.24) * mm, v(-6.25, -20.46) * mm, v(-6.48, -20) * mm, v(-6.89, -20.05) * mm, v(-7.6, -20.16) * mm, v(-8.26, -20.16) * mm, v(-9, -20.08) * mm, v(-10.01, -19.86) * mm, v(-10.83, -19.49) * mm, v(-11.5, -18.6) * mm, v(-11.76, -17.77) * mm, v(-11.76, -16.92) * mm, v(-11.46, -15.99) * mm, v(-10.9, -14.87) * mm, v(-10.12, -13.75) * mm, v(-10.38, -13.34) * mm, v(-10.94, -12.64) * mm, v(-11.39, -11.7) * mm, v(-11.72, -10.89) * mm, v(-11.72, -9.47) * mm, v(-11.35, -8.65) * mm, v(-10.94, -8.17) * mm, v(-9.9, -7.54) * mm, v(-8.6, -7.39) * mm, v(-7.48, -7.39) * mm, v(-6.51, -7.39) * mm]});
            skSolve(sketch);
        }
        {
            var Q0;
            Q0=makeQuery(id+"F5.imprint","IMPRINT",FACE,{"disambiguationData":[TD([[makeQuery(id+"F5.imprint","IMPRINT",EDGE,{"derivedFrom":sQuery(id+"F5.wireOp",EDGE,"E12")}),1.0]])]});
            var Q1;
            Q1=makeQuery(id+"F5.imprint","IMPRINT",FACE,{"disambiguationData":[TD([[makeQuery(id+"F5.imprint","IMPRINT",EDGE,{"derivedFrom":sQuery(id+"F5.wireOp",EDGE,"E11")}),1.0]])]});
            extrude(context, id + "F6", {"entities" : qUnion([Q0, Q1]), "operationType" : NewBodyOperationType.ADD, "depth" : 3.17 * mm, "offsetDistance" : 25.4 * mm});
        }
        {
            var Q0;
            {var subQ0=sQuery(id+"F0.wireOp",EDGE,"E8.sketch_text.stroke-52");var subQ1=sQuery(id+"F0.wireOp",EDGE,"E8.sketch_text.stroke-51");var subQ2=sQuery(id+"F0.wireOp",EDGE,"E8.sketch_text.stroke-50");var subQ3=sQuery(id+"F0.wireOp",EDGE,"E8.sketch_text.stroke-49");var subQ4=sQuery(id+"F0.wireOp",EDGE,"E8.sketch_text.stroke-48");var subQ5=sQuery(id+"F0.wireOp",EDGE,"E8.sketch_text.stroke-47");var subQ6=sQuery(id+"F0.wireOp",EDGE,"E8.sketch_text.stroke-46");var subQ7=sQuery(id+"F0.wireOp",EDGE,"E8.sketch_text.stroke-45");var subQ8=sQuery(id+"F0.wireOp",EDGE,"E8.sketch_text.stroke-44");var subQ9=sQuery(id+"F0.wireOp",EDGE,"E8.sketch_text.stroke-43");var subQ10=sQuery(id+"F0.wireOp",EDGE,"E8.sketch_text.stroke-42");var subQ11=sQuery(id+"F0.wireOp",EDGE,"E8.sketch_text.stroke-41");var subQ12=sQuery(id+"F0.wireOp",EDGE,"E8.sketch_text.stroke-40");var subQ13=sQuery(id+"F0.wireOp",EDGE,"E8.sketch_text.stroke-39");var subQ14=sQuery(id+"F0.wireOp",EDGE,"E8.sketch_text.stroke-38");var subQ15=sQuery(id+"F0.wireOp",EDGE,"E8.sketch_text.stroke-37");var subQ16=sQuery(id+"F0.wireOp",EDGE,"E8.sketch_text.stroke-36");var subQ17=sQuery(id+"F0.wireOp",EDGE,"E8.sketch_text.stroke-35");var subQ18=sQuery(id+"F0.wireOp",EDGE,"E8.sketch_text.stroke-34");var subQ19=sQuery(id+"F0.wireOp",EDGE,"E8.sketch_text.stroke-33");var subQ20=sQuery(id+"F0.wireOp",EDGE,"E8.sketch_text.stroke-32");var subQ21=sQuery(id+"F0.wireOp",EDGE,"E8.sketch_text.stroke-31");var subQ22=sQuery(id+"F0.wireOp",EDGE,"E8.sketch_text.stroke-30");var subQ23=sQuery(id+"F0.wireOp",EDGE,"E8.sketch_text.stroke-29");var subQ24=sQuery(id+"F0.wireOp",EDGE,"E8.sketch_text.stroke-28");var subQ25=sQuery(id+"F0.wireOp",EDGE,"E8.sketch_text.stroke-9");var subQ26=sQuery(id+"F0.wireOp",EDGE,"E8.sketch_text.stroke-8");var subQ27=sQuery(id+"F0.wireOp",EDGE,"E8.sketch_text.stroke-7");var subQ28=sQuery(id+"F0.wireOp",EDGE,"E8.sketch_text.stroke-6");var subQ29=sQuery(id+"F0.wireOp",EDGE,"E8.sketch_text.stroke-5");var subQ30=sQuery(id+"F0.wireOp",EDGE,"E8.sketch_text.stroke-4");var subQ31=sQuery(id+"F0.wireOp",EDGE,"E8.sketch_text.stroke-0");var subQ32=sQuery(id+"F0.wireOp",EDGE,"E4.filletArc");var subQ33=sQuery(id+"F0.wireOp",EDGE,"E8.sketch_text.stroke-1");var subQ34=sQuery(id+"F0.wireOp",EDGE,"E5.filletArc");var subQ35=sQuery(id+"F0.wireOp",EDGE,"E8.sketch_text.stroke-2");var subQ36=sQuery(id+"F0.wireOp",EDGE,"E6.filletArc");var subQ37=sQuery(id+"F0.wireOp",EDGE,"E8.sketch_text.stroke-3");var subQ38=sQuery(id+"F0.wireOp",EDGE,"E7.filletArc");var subQ39=sQuery(id+"F0.wireOp",EDGE,"E8.sketch_text.stroke-10");var subQ40=sQuery(id+"F0.wireOp",EDGE,"E8.sketch_text.stroke-11");var subQ41=sQuery(id+"F0.wireOp",EDGE,"E8.sketch_text.stroke-12");var subQ42=sQuery(id+"F0.wireOp",EDGE,"E8.sketch_text.stroke-13");var subQ43=sQuery(id+"F0.wireOp",EDGE,"E8.sketch_text.stroke-14");var subQ44=sQuery(id+"F0.wireOp",EDGE,"E8.sketch_text.stroke-15");var subQ45=sQuery(id+"F0.wireOp",EDGE,"E8.sketch_text.stroke-20");var subQ46=sQuery(id+"F0.wireOp",EDGE,"E8.sketch_text.stroke-21");var subQ47=sQuery(id+"F0.wireOp",EDGE,"E8.sketch_text.stroke-22");var subQ48=sQuery(id+"F0.wireOp",EDGE,"E8.sketch_text.stroke-23");var subQ49=sQuery(id+"F0.wireOp",EDGE,"E8.sketch_text.stroke-24");var subQ50=sQuery(id+"F0.wireOp",EDGE,"E8.sketch_text.stroke-27");var subQ51=sQuery(id+"F0.wireOp",EDGE,"E8.sketch_text.stroke-26");var subQ52=sQuery(id+"F0.wireOp",EDGE,"E8.sketch_text.stroke-25");var subQ53=sQuery(id+"F0.wireOp",EDGE,"E8.sketch_text.stroke-53");var subQ54=sQuery(id+"F0.wireOp",EDGE,"E8.sketch_text.stroke-54");var subQ55=sQuery(id+"F0.wireOp",EDGE,"E8.sketch_text.stroke-55");var subQ56=sQuery(id+"F0.wireOp",EDGE,"E8.sketch_text.stroke-56");var subQ57=sQuery(id+"F0.wireOp",EDGE,"E8.sketch_text.stroke-57");var subQ58=sQuery(id+"F0.wireOp",EDGE,"E8.sketch_text.stroke-58");var subQ59=sQuery(id+"F0.wireOp",EDGE,"E8.sketch_text.stroke-59");var subQ60=sQuery(id+"F0.wireOp",EDGE,"E8.sketch_text.stroke-60");var subQ61=sQuery(id+"F0.wireOp",EDGE,"E8.sketch_text.stroke-61");var subQ62=sQuery(id+"F0.wireOp",EDGE,"E8.sketch_text.stroke-62");var subQ63=sQuery(id+"F0.wireOp",EDGE,"E8.sketch_text.stroke-63");var subQ64=sQuery(id+"F0.wireOp",EDGE,"E8.sketch_text.stroke-64");var subQ65=sQuery(id+"F0.wireOp",EDGE,"E8.sketch_text.stroke-65");var subQ66=sQuery(id+"F0.wireOp",EDGE,"E8.sketch_text.stroke-66");var subQ67=sQuery(id+"F0.wireOp",EDGE,"E8.sketch_text.stroke-67");var subQ68=sQuery(id+"F0.wireOp",EDGE,"E8.sketch_text.stroke-68");var subQ69=sQuery(id+"F0.wireOp",EDGE,"E8.sketch_text.stroke-69");var subQ70=sQuery(id+"F0.wireOp",EDGE,"E8.sketch_text.stroke-70");var subQ71=sQuery(id+"F0.wireOp",EDGE,"E8.sketch_text.stroke-71");var subQ72=sQuery(id+"F0.wireOp",EDGE,"E8.sketch_text.stroke-72");var subQ73=sQuery(id+"F0.wireOp",EDGE,"E8.sketch_text.stroke-73");var subQ74=sQuery(id+"F0.wireOp",EDGE,"E8.sketch_text.stroke-74");var subQ75=sQuery(id+"F0.wireOp",EDGE,"E8.sketch_text.stroke-75");var subQ76=sQuery(id+"F0.wireOp",EDGE,"E8.sketch_text.stroke-76");var subQ77=sQuery(id+"F0.wireOp",EDGE,"E8.sketch_text.stroke-77");var subQ78=sQuery(id+"F0.wireOp",EDGE,"E8.sketch_text.stroke-78");var subQ79=sQuery(id+"F0.wireOp",EDGE,"E8.sketch_text.stroke-79");var subQ80=sQuery(id+"F0.wireOp",EDGE,"E8.sketch_text.stroke-80");var subQ81=sQuery(id+"F0.wireOp",EDGE,"E8.sketch_text.stroke-81");var subQ82=sQuery(id+"F0.wireOp",EDGE,"E8.sketch_text.stroke-82");var subQ83=sQuery(id+"F0.wireOp",EDGE,"E8.sketch_text.stroke-83");var subQ84=sQuery(id+"F0.wireOp",EDGE,"E8.sketch_text.stroke-84");var subQ85=sQuery(id+"F0.wireOp",EDGE,"E0");var subQ86=sQuery(id+"F0.wireOp",EDGE,"E1");var subQ87=sQuery(id+"F0.wireOp",EDGE,"E2");var subQ88=sQuery(id+"F0.wireOp",EDGE,"E3");Q0=makeQuery(id+"F6.boolean.opBoolean","SPLIT",FACE,{"disambiguationData":[TD([makeQuery(id+"F1.opExtrude","SWEPT_FACE",FACE,{"disambiguationData":[OSD([subQ31])]})])],"derivedFrom":makeQuery(id+"F1.opExtrude","CAP_FACE",FACE,{"disambiguationData":[OSD([subQ85,subQ86,subQ87,subQ88,subQ32,subQ34,subQ36,subQ38,subQ31,subQ33,subQ35,subQ37,subQ30,subQ29,subQ28,subQ27,subQ26,subQ25,subQ39,subQ40,subQ41,subQ42,subQ43,subQ44,subQ45,subQ46,subQ47,subQ48,subQ49,subQ52,subQ51,subQ50,subQ24,subQ23,subQ22,subQ21,subQ20,subQ19,subQ18,subQ17,subQ16,subQ15,subQ14,subQ13,subQ12,subQ11,subQ10,subQ9,subQ8,subQ7,subQ6,subQ5,subQ4,subQ3,subQ2,subQ1,subQ0,subQ53,subQ54,subQ55,subQ56,subQ57,subQ58,subQ59,subQ60,subQ61,subQ62,subQ63,subQ64,subQ65,subQ66,subQ67,subQ68,subQ69,subQ70,subQ71,subQ72,subQ73,subQ74,subQ75,subQ76,subQ77,subQ78,subQ79,subQ80,subQ81,subQ82,subQ83,subQ84])],"isStart":false})});}
            var sketch = newSketch(context, id + "F7", { "sketchPlane" : qUnion([Q0])});
            skLineSegment(sketch, "E26", {"start": v(20.93, -13.29) * mm, "end": v(17.35, -14) * mm});
            skLineSegment(sketch, "E27", {"start": v(17.35, -14) * mm, "end": v(17.35, -19.58) * mm});
            skLineSegment(sketch, "E28", {"start": v(17.35, -19.58) * mm, "end": v(16.33, -19.58) * mm});
            skLineSegment(sketch, "E29", {"start": v(16.33, -19.58) * mm, "end": v(16.33, -21) * mm});
            skLineSegment(sketch, "E30", {"start": v(16.33, -21) * mm, "end": v(38.5, -21) * mm});
            skLineSegment(sketch, "E31", {"start": v(38.5, -21) * mm, "end": v(38.5, -19.58) * mm});
            skLineSegment(sketch, "E32", {"start": v(38.5, -19.58) * mm, "end": v(37.62, -19.58) * mm});
            skLineSegment(sketch, "E33", {"start": v(37.62, -19.58) * mm, "end": v(37.62, -14.7) * mm});
            skLineSegment(sketch, "E34", {"start": v(37.62, -14.7) * mm, "end": v(35.14, -14.7) * mm});
            skLineSegment(sketch, "E35", {"start": v(35.14, -14.7) * mm, "end": v(35.14, -12.27) * mm});
            skLineSegment(sketch, "E36", {"start": v(35.14, -12.27) * mm, "end": v(31.56, -11.65) * mm});
            skLineSegment(sketch, "E37", {"start": v(31.56, -11.65) * mm, "end": v(31.56, -8.46) * mm});
            skLineSegment(sketch, "E38", {"start": v(31.56, -8.46) * mm, "end": v(31.16, -8.46) * mm});
            skLineSegment(sketch, "E39", {"start": v(28.15, -8.42) * mm, "end": v(27.75, -8.42) * mm});
            skLineSegment(sketch, "E40", {"start": v(27.75, -8.42) * mm, "end": v(27.75, -14.66) * mm});
            skLineSegment(sketch, "E41", {"start": v(27.75, -14.66) * mm, "end": v(27, -14.66) * mm});
            skLineSegment(sketch, "E42", {"start": v(27, -14.66) * mm, "end": v(27, -10.8) * mm});
            skLineSegment(sketch, "E43", {"start": v(27, -10.8) * mm, "end": v(26.02, -10.8) * mm});
            skLineSegment(sketch, "E44", {"start": v(26.02, -10.8) * mm, "end": v(26.02, -9.8) * mm});
            skLineSegment(sketch, "E45", {"start": v(26.02, -9.8) * mm, "end": v(21.82, -9.8) * mm});
            skLineSegment(sketch, "E46", {"start": v(21.82, -9.8) * mm, "end": v(21.82, -10.68) * mm});
            skLineSegment(sketch, "E47", {"start": v(21.82, -10.68) * mm, "end": v(21.02, -10.68) * mm});
            skLineSegment(sketch, "E48", {"start": v(21.02, -10.68) * mm, "end": v(20.93, -13.29) * mm});
            skArc(sketch, "E49", {"start": v(29.3, -7.1) * mm, "mid": v(28.46, -7.53) * mm, "end": v(28.15, -8.42) * mm});
            skArc(sketch, "E50", {"start": v(31.16, -8.46) * mm, "mid": v(30.8, -7.52) * mm, "end": v(29.92, -7.05) * mm});
            skLineSegment(sketch, "E51", {"start": v(29.3, -7.1) * mm, "end": v(29.3, -5.54) * mm});
            skLineSegment(sketch, "E52", {"start": v(29.3, -5.54) * mm, "end": v(29.96, -5.54) * mm});
            skLineSegment(sketch, "E53", {"start": v(29.96, -5.54) * mm, "end": v(29.92, -7.05) * mm});
            skLineSegment(sketch, "E54", {"start": v(21.99, -11.86) * mm, "end": v(22.78, -11.86) * mm});
            skLineSegment(sketch, "E55", {"start": v(22.78, -11.86) * mm, "end": v(22.78, -12.66) * mm});
            skLineSegment(sketch, "E56", {"start": v(22.78, -12.66) * mm, "end": v(21.98, -12.66) * mm});
            skLineSegment(sketch, "E57", {"start": v(21.98, -12.66) * mm, "end": v(21.99, -11.86) * mm});
            skLineSegment(sketch, "E58", {"start": v(21.99, -13.46) * mm, "end": v(22.78, -13.46) * mm});
            skLineSegment(sketch, "E59", {"start": v(22.78, -13.46) * mm, "end": v(22.78, -14.24) * mm});
            skLineSegment(sketch, "E60", {"start": v(22.78, -14.24) * mm, "end": v(21.99, -14.24) * mm});
            skLineSegment(sketch, "E61", {"start": v(21.99, -14.24) * mm, "end": v(21.99, -13.46) * mm});
            skLineSegment(sketch, "E62", {"start": v(19.54, -15.04) * mm, "end": v(20.35, -15.04) * mm});
            skLineSegment(sketch, "E63", {"start": v(20.35, -15.04) * mm, "end": v(20.35, -15.83) * mm});
            skLineSegment(sketch, "E64", {"start": v(20.35, -15.83) * mm, "end": v(19.54, -15.83) * mm});
            skLineSegment(sketch, "E65", {"start": v(19.54, -15.83) * mm, "end": v(19.54, -15.04) * mm});
            skLineSegment(sketch, "E66", {"start": v(21.99, -15.04) * mm, "end": v(22.75, -15.04) * mm});
            skLineSegment(sketch, "E67", {"start": v(22.75, -15.04) * mm, "end": v(22.75, -15.8) * mm});
            skLineSegment(sketch, "E68", {"start": v(22.75, -15.8) * mm, "end": v(21.99, -15.8) * mm});
            skLineSegment(sketch, "E69", {"start": v(21.99, -15.8) * mm, "end": v(21.99, -15.04) * mm});
            skLineSegment(sketch, "E70", {"start": v(25.38, -16.65) * mm, "end": v(26.13, -16.65) * mm});
            skLineSegment(sketch, "E71", {"start": v(26.13, -16.65) * mm, "end": v(26.13, -17.43) * mm});
            skLineSegment(sketch, "E72", {"start": v(25.38, -16.65) * mm, "end": v(25.38, -17.43) * mm});
            skLineSegment(sketch, "E73", {"start": v(25.38, -17.43) * mm, "end": v(26.13, -17.43) * mm});
            skLineSegment(sketch, "E74", {"start": v(25.38, -18.23) * mm, "end": v(26.13, -18.23) * mm});
            skLineSegment(sketch, "E75", {"start": v(26.13, -18.23) * mm, "end": v(26.13, -19.05) * mm});
            skLineSegment(sketch, "E76", {"start": v(26.13, -19.05) * mm, "end": v(25.38, -19.05) * mm});
            skLineSegment(sketch, "E77", {"start": v(25.38, -19.05) * mm, "end": v(25.38, -18.23) * mm});
            skLineSegment(sketch, "E78", {"start": v(33.2, -15.22) * mm, "end": v(33.96, -15.22) * mm});
            skLineSegment(sketch, "E79", {"start": v(33.96, -15.22) * mm, "end": v(33.96, -16) * mm});
            skLineSegment(sketch, "E80", {"start": v(33.96, -16) * mm, "end": v(33.2, -16) * mm});
            skLineSegment(sketch, "E81", {"start": v(33.2, -16) * mm, "end": v(33.2, -15.22) * mm});
            skLineSegment(sketch, "E82", {"start": v(33.2, -13.29) * mm, "end": v(33.95, -13.29) * mm});
            skLineSegment(sketch, "E83", {"start": v(33.95, -13.29) * mm, "end": v(33.95, -14.05) * mm});
            skLineSegment(sketch, "E84", {"start": v(33.95, -14.05) * mm, "end": v(33.2, -14.03) * mm});
            skLineSegment(sketch, "E85", {"start": v(33.2, -14.03) * mm, "end": v(33.2, -13.29) * mm});
            skLineSegment(sketch, "E86", {"start": v(28.63, -9.78) * mm, "end": v(29.4, -9.78) * mm});
            skLineSegment(sketch, "E87", {"start": v(29.4, -9.78) * mm, "end": v(29.4, -10.52) * mm});
            skLineSegment(sketch, "E88", {"start": v(29.4, -10.52) * mm, "end": v(28.62, -10.52) * mm});
            skLineSegment(sketch, "E89", {"start": v(28.62, -10.52) * mm, "end": v(28.63, -9.78) * mm});
            skLineSegment(sketch, "E90", {"start": v(28.63, -11.37) * mm, "end": v(29.41, -11.37) * mm});
            skLineSegment(sketch, "E91", {"start": v(29.41, -11.37) * mm, "end": v(29.41, -12.1) * mm});
            skLineSegment(sketch, "E92", {"start": v(29.41, -12.1) * mm, "end": v(28.63, -12.1) * mm});
            skLineSegment(sketch, "E93", {"start": v(28.63, -12.1) * mm, "end": v(28.63, -11.37) * mm});
            skSolve(sketch);
        }
        {
            var Q0;
            Q0=makeQuery(id+"F7.imprint","IMPRINT",FACE,{"disambiguationData":[TD([[makeQuery(id+"F7.imprint","IMPRINT",EDGE,{"derivedFrom":sQuery(id+"F7.wireOp",EDGE,"E26")}),1.0]])]});
            extrude(context, id + "F8", {"entities" : qUnion([Q0]), "operationType" : NewBodyOperationType.ADD, "depth" : 3.17 * mm, "offsetDistance" : 25.4 * mm});
        }
        {
            var Q0;
            Q0=makeQuery(id+"F0.imprint","IMPRINT",FACE,{"disambiguationData":[TD([[makeQuery(id+"F0.imprint","IMPRINT",EDGE,{"derivedFrom":sQuery(id+"F0.wireOp",EDGE,"E8.sketch_text.stroke-0")}),-1.0]])]});
            var Q1;
            Q1=makeQuery(id+"F0.imprint","IMPRINT",FACE,{"disambiguationData":[TD([[makeQuery(id+"F0.imprint","IMPRINT",EDGE,{"derivedFrom":sQuery(id+"F0.wireOp",EDGE,"E8.sketch_text.stroke-20")}),-1.0]])]});
            var Q2;
            Q2=makeQuery(id+"F0.imprint","IMPRINT",FACE,{"disambiguationData":[TD([[makeQuery(id+"F0.imprint","IMPRINT",EDGE,{"derivedFrom":sQuery(id+"F0.wireOp",EDGE,"E8.sketch_text.stroke-36")}),-1.0]])]});
            var Q3;
            Q3=makeQuery(id+"F0.imprint","IMPRINT",FACE,{"disambiguationData":[TD([[makeQuery(id+"F0.imprint","IMPRINT",EDGE,{"derivedFrom":sQuery(id+"F0.wireOp",EDGE,"E8.sketch_text.stroke-57")}),-1.0]])]});
            extrude(context, id + "F9", {"entities" : qUnion([Q0, Q1, Q2, Q3]), "operationType" : NewBodyOperationType.ADD, "depth" : 3.17 * mm, "offsetDistance" : 25.4 * mm});
        }
        {
            var Q0;
            Q0=makeQuery(id+"F0.imprint","IMPRINT",FACE,{"disambiguationData":[TD([[makeQuery(id+"F0.imprint","IMPRINT",EDGE,{"derivedFrom":sQuery(id+"F0.wireOp",EDGE,"E8.sketch_text.stroke-16")}),1.0]])]});
            extrude(context, id + "F10", {"entities" : qUnion([Q0]), "operationType" : NewBodyOperationType.ADD, "depth" : 8.25 * mm, "offsetDistance" : 25.4 * mm});
        }
    });
